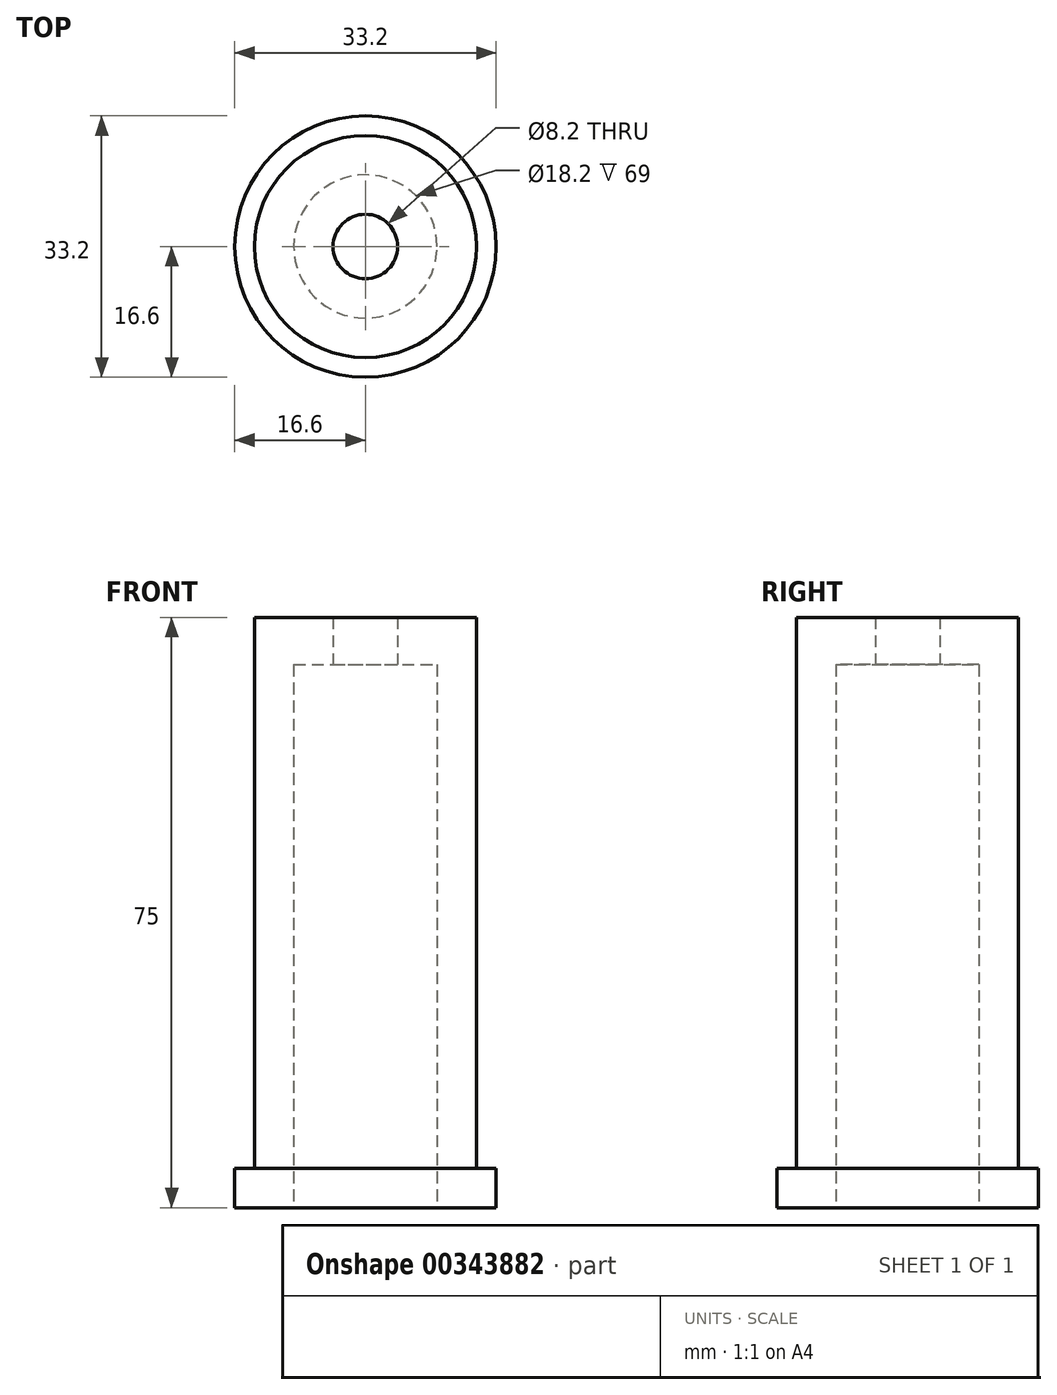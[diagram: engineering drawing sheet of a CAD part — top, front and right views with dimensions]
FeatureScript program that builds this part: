
annotation { "Feature Type Name" : "Feature", "Feature Type Description" : "" }
export const myFeature = defineFeature(function(context is Context, id is Id, definition is map)
    precondition{}
    {
        {
            var Q0;
            Q0=qCreatedBy(makeId("Front.planeOp"),FACE);
            var sketch = newSketch(context, id + "F0", { "sketchPlane" : qUnion([Q0])});
            skLineSegment(sketch, "E0", {"start": v(16.6, 0) * mm, "end": v(9.1, 0) * mm});
            skLineSegment(sketch, "E1", {"start": v(9.1, 0) * mm, "end": v(9.1, 69) * mm});
            skLineSegment(sketch, "E2", {"start": v(16.6, 0) * mm, "end": v(16.6, 5) * mm});
            skLineSegment(sketch, "E3", {"start": v(16.6, 5) * mm, "end": v(14.1, 5) * mm});
            skLineSegment(sketch, "E4", {"start": v(14.1, 5) * mm, "end": v(14.1, 75) * mm});
            skLineSegment(sketch, "E5", {"start": v(9.1, 69) * mm, "end": v(4.1, 69) * mm});
            skLineSegment(sketch, "E6", {"start": v(0, 0) * mm, "end": v(0, 76.62) * mm, "construction": true});
            skLineSegment(sketch, "E7", {"start": v(14.1, 75) * mm, "end": v(4.1, 75) * mm});
            skLineSegment(sketch, "E8", {"start": v(4.1, 75) * mm, "end": v(4.1, 69) * mm});
            skSolve(sketch);
        }
        {
            var Q0;
            Q0=makeQuery(id+"F0.imprint","IMPRINT",FACE,{"disambiguationData":[TD([[makeQuery(id+"F0.imprint","IMPRINT",EDGE,{"derivedFrom":sQuery(id+"F0.wireOp",EDGE,"E0")}),-1.0]])]});
            var Q1;
            Q1=sQuery(id+"F0.wireOp",EDGE,"E6");
            revolve(context, id + "F1", {"entities" : qUnion([Q0]), "axis" : qUnion([Q1]), "revolveType" : RevolveType.FULL});
        }
    });
